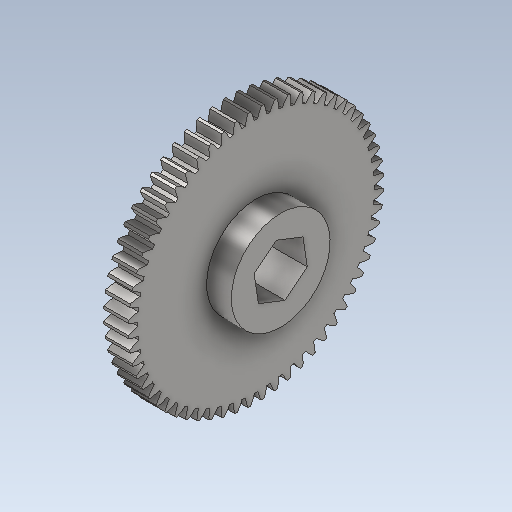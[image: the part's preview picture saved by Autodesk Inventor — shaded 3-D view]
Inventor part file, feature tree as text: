
AUTODESK INVENTOR PART (.ipt)
format: ipt  version: 2023 (Build 270158000, 158)  size: 1,077,760 bytes
history: native  units: in
note: dims shown in document units (in); Inventor stores cm internally (conversion verified against a paired STEP export)
features: sketch x3, projected_geometry x2, revolve x1, extrude x1, hole x1, fillet x1, other x1
ambient origin geometry x8: Origin, YZ Plane, XZ Plane, XY Plane, X Axis, Y Axis, Z Axis, Center Point
bodies: Solid1 (feature_tree)
feature tree (10):
  revolve  "Revolution1"  [1 undecoded]
  extrude  "Extrusion3"  Depth=0.1875in
  hole  "Hole1"  [1 undecoded]
  fillet  "Fillet1"  Radius=0.375in
  sketch  "Sketch3"  dims[d6=0.25in d7=0.1875in]
  projected_geometry  "Projected Loop1"
  sketch  "Sketch4"  dims[d8=0.1875in d10=0.125in]
  projected_geometry  "Projected Loop2"
  sketch  "Sketch5"  dims[d11=90.0deg d12=0.0625in d13=0.13in d14=0.328in d15=0.375in d16=0.25in d17=0.5635in d18=1.0in d19=0.8108in d20=0.375in d21=0.0in d22=0.0in]
  other  "TeethCuts"
note: 2 required parameter values undecoded (feature->parameter linkage not recoverable at this tier; creation-order binding heuristic only, values carry confidence <= 0.55)